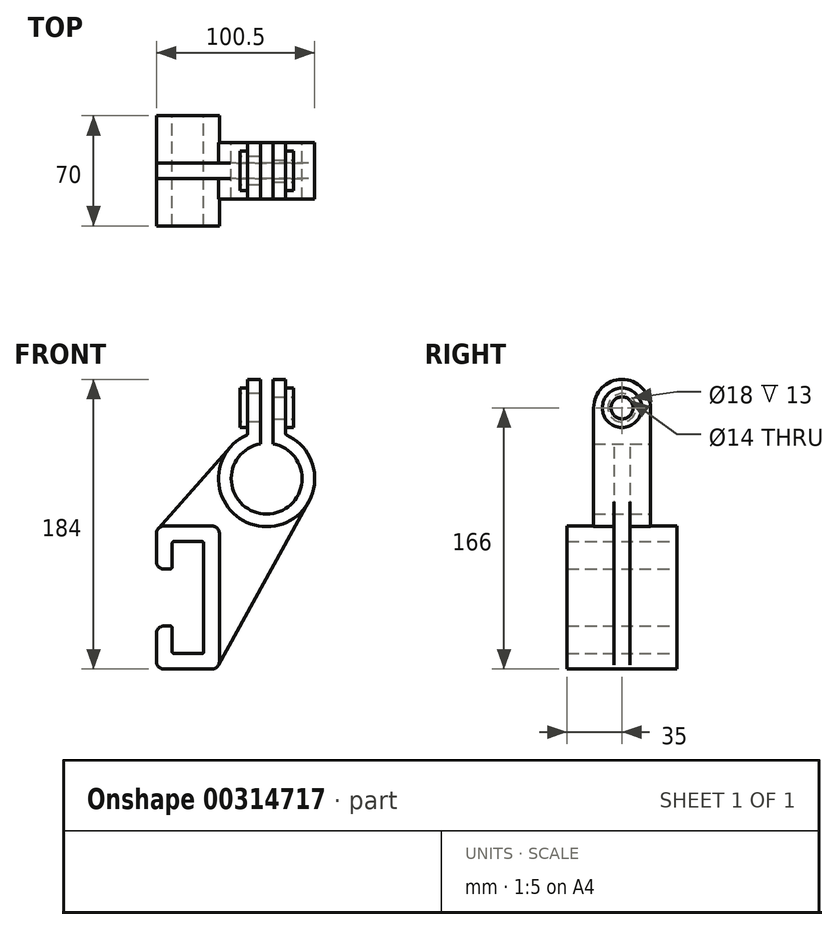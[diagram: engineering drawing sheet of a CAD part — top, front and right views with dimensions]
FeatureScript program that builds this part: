
annotation { "Feature Type Name" : "Feature", "Feature Type Description" : "" }
export const myFeature = defineFeature(function(context is Context, id is Id, definition is map)
    precondition{}
    {
        {
            var Q0;
            Q0=qCreatedBy(makeId("Front.planeOp"),FACE);
            var sketch = newSketch(context, id + "F0", { "sketchPlane" : qUnion([Q0])});
            skArc(sketch, "E0", {"start": v(-4, 22.14) * mm, "mid": v(0, -22.5) * mm, "end": v(4, 22.14) * mm});
            skLineSegment(sketch, "E1", {"start": v(0, 0) * mm, "end": v(0, 45) * mm, "construction": true});
            skLineSegment(sketch, "E2.0", {"start": v(-4, 22.14) * mm, "end": v(-4, 45) * mm});
            skLineSegment(sketch, "E3.0", {"start": v(4, 22.14) * mm, "end": v(4, 45) * mm});
            skLineSegment(sketch, "E4.0", {"start": v(12, 28.04) * mm, "end": v(12, 45) * mm});
            skArc(sketch, "E4.1", {"start": v(-12, 28.04) * mm, "mid": v(0, -30.5) * mm, "end": v(12, 28.04) * mm});
            skLineSegment(sketch, "E4.2", {"start": v(-12, 28.04) * mm, "end": v(-12, 45) * mm});
            skLineSegment(sketch, "E5", {"start": v(-12, 45) * mm, "end": v(-4, 45) * mm});
            skLineSegment(sketch, "E6", {"start": v(4, 45) * mm, "end": v(12, 45) * mm});
            skLineSegment(sketch, "E7.bottom", {"start": v(-40, -40) * mm, "end": v(-60, -40) * mm});
            skLineSegment(sketch, "E7.top", {"start": v(-40, -111) * mm, "end": v(-60, -111) * mm});
            skLineSegment(sketch, "E7.left", {"start": v(-40, -40) * mm, "end": v(-40, -111) * mm});
            skLineSegment(sketch, "E7.right", {"start": v(-60, -40) * mm, "end": v(-60, -57.5) * mm});
            skLineSegment(sketch, "E8.0", {"start": v(-70, -35) * mm, "end": v(-70, -52.5) * mm});
            skLineSegment(sketch, "E8.1", {"start": v(-35, -30) * mm, "end": v(-65, -30) * mm});
            skLineSegment(sketch, "E8.2", {"start": v(-30, -35) * mm, "end": v(-30, -116) * mm});
            skLineSegment(sketch, "E8.3", {"start": v(-35, -121) * mm, "end": v(-65, -121) * mm});
            skLineSegment(sketch, "E9", {"start": v(-60, -40) * mm, "end": v(-40, -111) * mm, "construction": true});
            skLineSegment(sketch, "E10.left", {"start": v(-100, -57.5) * mm, "end": v(-100, -93.5) * mm, "construction": true});
            skLineSegment(sketch, "E10.right", {"start": v(0, -57.5) * mm, "end": v(0, -93.5) * mm, "construction": true});
            skPoint(sketch, "E10.middle", {"position": v(-50, -75.5) * mm});
            skLineSegment(sketch, "E11.trimOffspring", {"start": v(-70, -98.5) * mm, "end": v(-70, -116) * mm});
            skLineSegment(sketch, "E12.trimOffspring", {"start": v(-60, -93.5) * mm, "end": v(-60, -111) * mm});
            skLineSegment(sketch, "E13", {"start": v(-65, -57.5) * mm, "end": v(-60, -57.5) * mm});
            skLineSegment(sketch, "E14", {"start": v(-65, -93.5) * mm, "end": v(-60, -93.5) * mm});
            skPoint(sketch, "E15.visualSharp", {"position": v(-70, -30) * mm});
            skArc(sketch, "E15.filletArc", {"start": v(-65, -30) * mm, "mid": v(-68.54, -31.46) * mm, "end": v(-70, -35) * mm});
            skPoint(sketch, "E16.visualSharp", {"position": v(-30, -30) * mm});
            skArc(sketch, "E16.filletArc", {"start": v(-30, -35) * mm, "mid": v(-31.46, -31.46) * mm, "end": v(-35, -30) * mm});
            skPoint(sketch, "E17.visualSharp", {"position": v(-30, -121) * mm});
            skArc(sketch, "E17.filletArc", {"start": v(-35, -121) * mm, "mid": v(-31.46, -119.54) * mm, "end": v(-30, -116) * mm});
            skPoint(sketch, "E18.visualSharp", {"position": v(-70, -121) * mm});
            skArc(sketch, "E18.filletArc", {"start": v(-70, -116) * mm, "mid": v(-68.54, -119.54) * mm, "end": v(-65, -121) * mm});
            skPoint(sketch, "E19.newPointB", {"position": v(-100, -93.5) * mm});
            skArc(sketch, "E19.filletArc", {"start": v(-65, -93.5) * mm, "mid": v(-68.54, -94.96) * mm, "end": v(-70, -98.5) * mm});
            skPoint(sketch, "E20.newPointB", {"position": v(-100, -57.5) * mm});
            skArc(sketch, "E20.filletArc", {"start": v(-70, -52.5) * mm, "mid": v(-68.54, -56.04) * mm, "end": v(-65, -57.5) * mm});
            skLineSegment(sketch, "E21.trimOffspring", {"start": v(-100, -57.5) * mm, "end": v(0, -57.5) * mm, "construction": true});
            skLineSegment(sketch, "E22.trimOffspring", {"start": v(-100, -93.5) * mm, "end": v(0, -93.5) * mm, "construction": true});
            skLineSegment(sketch, "E23", {"start": v(-22.85, 20.2) * mm, "end": v(-68.75, -31.69) * mm});
            skLineSegment(sketch, "E24", {"start": v(26.7, -14.76) * mm, "end": v(-30.62, -118.42) * mm});
            skSolve(sketch);
        }
        {
            var Q0;
            Q0=makeQuery(id+"F0.imprint","IMPRINT",FACE,{"disambiguationData":[TD([[makeQuery(id+"F0.imprint","IMPRINT",EDGE,{"derivedFrom":sQuery(id+"F0.wireOp",EDGE,"E0")}),-1.0]])]});
            extrude(context, id + "F1", {"entities" : qUnion([Q0]), "endBound" : BoundingType.SYMMETRIC, "depth" : 36 * mm});
        }
        {
            var Q0;
            {var subQ1=sQuery(id+"F0.wireOp",EDGE,"E8.1");Q0=makeQuery(id+"F0.imprint","IMPRINT",FACE,{"disambiguationData":[TD([[makeQuery(id+"F0.imprint","IMPRINT",EDGE,{"derivedFrom":subQ1}),-1.0]])]});}
            extrude(context, id + "F2", {"entities" : qUnion([Q0]), "operationType" : NewBodyOperationType.ADD, "endBound" : BoundingType.SYMMETRIC, "depth" : 10 * mm});
        }
        {
            var Q0;
            Q0=makeQuery(id+"F0.imprint","IMPRINT",FACE,{"disambiguationData":[TD([[makeQuery(id+"F0.imprint","IMPRINT",EDGE,{"derivedFrom":sQuery(id+"F0.wireOp",EDGE,"E7.bottom")}),-1.0]])]});
            extrude(context, id + "F3", {"entities" : qUnion([Q0]), "operationType" : NewBodyOperationType.ADD, "endBound" : BoundingType.SYMMETRIC, "depth" : 70 * mm});
        }
        {
            var Q0;
            Q0=qCreatedBy(makeId("Right.planeOp"),FACE);
            var sketch = newSketch(context, id + "F4", { "sketchPlane" : qUnion([Q0])});
            skLineSegment(sketch, "E25.0", {"start": v(-18, 45) * mm, "end": v(18, 45) * mm});
            skArc(sketch, "E26", {"start": v(18, 45) * mm, "mid": v(0, 63) * mm, "end": v(-18, 45) * mm});
            skSolve(sketch);
        }
        {
            var Q0;
            Q0=makeQuery(id+"F1.opExtrude","SWEPT_FACE",FACE,{"disambiguationData":[OSD([sQuery(id+"F0.wireOp",EDGE,"E4.0")])]});
            var sketch = newSketch(context, id + "F5", { "sketchPlane" : qUnion([Q0])});
            skArc(sketch, "E27.0", {"start": v(18, 45) * mm, "mid": v(0, 63) * mm, "end": v(-18, 45) * mm});
            skLineSegment(sketch, "E28.0", {"start": v(-18, 45) * mm, "end": v(18, 45) * mm});
            skSolve(sketch);
        }
        {
            var Q0;
            Q0 = qSketchRegion(id + "F5", true);
            var Q1;
            Q1=makeQuery(id+"F1.opExtrude","SWEPT_FACE",FACE,{"disambiguationData":[OSD([sQuery(id+"F0.wireOp",EDGE,"E3.0")])]});
            extrude(context, id + "F6", {"entities" : qUnion([Q0]), "operationType" : NewBodyOperationType.ADD, "endBound" : BoundingType.UP_TO_SURFACE, "oppositeDirection" : true, "endBoundEntityFace" : qUnion([Q1]), "depth" : 25 * mm});
        }
        {
            var Q0;
            Q0=makeQuery(id+"F1.opExtrude","SWEPT_FACE",FACE,{"disambiguationData":[OSD([sQuery(id+"F0.wireOp",EDGE,"E4.2")])]});
            var sketch = newSketch(context, id + "F7", { "sketchPlane" : qUnion([Q0])});
            skLineSegment(sketch, "E29.0.0", {"start": v(18, 45) * mm, "end": v(-18, 45) * mm});
            skArc(sketch, "E29.0.1", {"start": v(-18, 45) * mm, "mid": v(0, 63) * mm, "end": v(18, 45) * mm});
            skSolve(sketch);
        }
        {
            var Q0;
            Q0=makeQuery(id+"F7.imprint","IMPRINT",FACE,{"disambiguationData":[TD([[makeQuery(id+"F7.imprint","IMPRINT",EDGE,{"derivedFrom":sQuery(id+"F7.wireOp",EDGE,"E29.0.0")}),-1.0]])]});
            var Q1;
            Q1=makeQuery(id+"F1.opExtrude","SWEPT_FACE",FACE,{"disambiguationData":[OSD([sQuery(id+"F0.wireOp",EDGE,"E2.0")])]});
            extrude(context, id + "F8", {"entities" : qUnion([Q0]), "operationType" : NewBodyOperationType.ADD, "endBound" : BoundingType.UP_TO_SURFACE, "oppositeDirection" : true, "endBoundEntityFace" : qUnion([Q1]), "depth" : 25 * mm});
        }
        {
            var Q0;
            Q0=makeQuery(id+"F8.boolean.opBoolean","MERGE",FACE,{"derivedFrom":[makeQuery(id+"F1.opExtrude","SWEPT_FACE",FACE,{"disambiguationData":[OSD([sQuery(id+"F0.wireOp",EDGE,"E4.2")])]}),makeQuery(id+"F8.opExtrude","CAP_FACE",FACE,{"disambiguationData":[OSD([sQuery(id+"F7.wireOp",EDGE,"E29.0.0"),sQuery(id+"F7.wireOp",EDGE,"E29.0.1")])],"isStart":true})]});
            var sketch = newSketch(context, id + "F9", { "sketchPlane" : qUnion([Q0])});
            skPoint(sketch, "E30", {"position": v(0, 45) * mm});
            skCircle(sketch, "E31", {"center": v(0, 45) * mm, "radius": 12.5 * mm});
            skSolve(sketch);
        }
        {
            var Q0;
            Q0=makeQuery(id+"F9.imprint","IMPRINT",FACE,{"disambiguationData":[TD([[makeQuery(id+"F9.imprint","IMPRINT",EDGE,{"derivedFrom":sQuery(id+"F9.wireOp",EDGE,"E31")}),1.0]])]});
            extrude(context, id + "F10", {"entities" : qUnion([Q0]), "operationType" : NewBodyOperationType.ADD, "depth" : 5 * mm});
        }
        {
            var Q0;
            Q0=makeQuery(id+"F6.boolean.opBoolean","MERGE",FACE,{"derivedFrom":[makeQuery(id+"F1.opExtrude","SWEPT_FACE",FACE,{"disambiguationData":[OSD([sQuery(id+"F0.wireOp",EDGE,"E4.0")])]}),makeQuery(id+"F6.opExtrude","CAP_FACE",FACE,{"disambiguationData":[OSD([sQuery(id+"F5.wireOp",EDGE,"E27.0"),sQuery(id+"F5.wireOp",EDGE,"E28.0")])],"isStart":true})]});
            var sketch = newSketch(context, id + "F11", { "sketchPlane" : qUnion([Q0])});
            skCircle(sketch, "E32.0", {"center": v(0, 45) * mm, "radius": 12.5 * mm});
            skSolve(sketch);
        }
        {
            var Q0;
            Q0=makeQuery(id+"F11.imprint","IMPRINT",FACE,{"disambiguationData":[TD([[makeQuery(id+"F11.imprint","IMPRINT",EDGE,{"derivedFrom":sQuery(id+"F11.wireOp",EDGE,"E32.0")}),1.0]])]});
            extrude(context, id + "F12", {"entities" : qUnion([Q0]), "operationType" : NewBodyOperationType.ADD, "depth" : 5 * mm});
        }
        {
            var Q0;
            Q0=makeQuery(id+"F10.opExtrude","CAP_FACE",FACE,{"disambiguationData":[OSD([sQuery(id+"F9.wireOp",EDGE,"E31")])],"isStart":false});
            var sketch = newSketch(context, id + "F13", { "sketchPlane" : qUnion([Q0])});
            skPoint(sketch, "E33", {"position": v(0, 45) * mm});
            skSolve(sketch);
        }
        {
            var Q0;
            Q0=sQuery(id+"F13.wireOp",VERTEX,"E33");
            var Q1;
            Q1=makeQuery(id+"F1.opExtrude","SWEPT_BODY",BODY,{"disambiguationData":[OSD([sQuery(id+"F0.wireOp",EDGE,"E0"),sQuery(id+"F0.wireOp",EDGE,"E2.0"),sQuery(id+"F0.wireOp",EDGE,"E3.0"),sQuery(id+"F0.wireOp",EDGE,"E4.0"),sQuery(id+"F0.wireOp",EDGE,"E4.1"),sQuery(id+"F0.wireOp",EDGE,"E4.2"),sQuery(id+"F0.wireOp",EDGE,"E5"),sQuery(id+"F0.wireOp",EDGE,"E6")])]});
            hole(context, id + "F14", {"style" : HoleStyle.SIMPLE, "endStyle" : HoleEndStyle.BLIND, "holeDiameter" : 18 * mm, "holeDepth" : 18 * mm, "tappedDepth" : 12 * mm, "tapClearance" : 3, "locations" : qUnion([Q0]), "scope" : qUnion([Q1])});
        }
        {
            var Q0;
            Q0=makeQuery(id+"F12.opExtrude","CAP_FACE",FACE,{"disambiguationData":[OSD([sQuery(id+"F11.wireOp",EDGE,"E32.0")])],"isStart":false});
            var sketch = newSketch(context, id + "F15", { "sketchPlane" : qUnion([Q0])});
            skPoint(sketch, "E34", {"position": v(0, 45) * mm});
            skSolve(sketch);
        }
        {
            var Q0;
            Q0=sQuery(id+"F15.wireOp",VERTEX,"E34");
            var Q1;
            Q1=makeQuery(id+"F1.opExtrude","SWEPT_BODY",BODY,{"disambiguationData":[OSD([sQuery(id+"F0.wireOp",EDGE,"E0"),sQuery(id+"F0.wireOp",EDGE,"E2.0"),sQuery(id+"F0.wireOp",EDGE,"E3.0"),sQuery(id+"F0.wireOp",EDGE,"E4.0"),sQuery(id+"F0.wireOp",EDGE,"E4.1"),sQuery(id+"F0.wireOp",EDGE,"E4.2"),sQuery(id+"F0.wireOp",EDGE,"E5"),sQuery(id+"F0.wireOp",EDGE,"E6")])]});
            hole(context, id + "F16", {"style" : HoleStyle.SIMPLE, "endStyle" : HoleEndStyle.BLIND, "standardTappedOrClearance" : lookupTablePath({ "standard" : "ISO", "engagement" : "75%", "pitch" : "2 mm", "size" : "M16", "type" : "Tapped" }), "standardBlindInLast" : lookupTablePath({ "standard" : "ISO", "engagement" : "75%", "pitch" : "2 mm", "size" : "M16", "type" : "Tapped" }), "holeDiameter" : 14 * mm, "showTappedDepth" : true, "holeDepth" : 18 * mm, "tappedDepth" : 12 * mm, "tapClearance" : 3, "locations" : qUnion([Q0]), "scope" : qUnion([Q1]), "majorDiameter" : 16 * mm});
        }
        {
            var Q0;
            Q0=makeQuery(id+"F3.opExtrude","SWEPT_EDGE",EDGE,{"disambiguationData":[OSD([sQuery(id+"F0.wireOp",EDGE,"E7.bottom"),sQuery(id+"F0.wireOp",EDGE,"E7.right")])]});
            var Q1;
            Q1=makeQuery(id+"F3.opExtrude","SWEPT_EDGE",EDGE,{"disambiguationData":[OSD([sQuery(id+"F0.wireOp",EDGE,"E7.bottom"),sQuery(id+"F0.wireOp",EDGE,"E7.left")])]});
            var Q2;
            Q2=makeQuery(id+"F3.opExtrude","SWEPT_EDGE",EDGE,{"disambiguationData":[OSD([sQuery(id+"F0.wireOp",EDGE,"E7.top"),sQuery(id+"F0.wireOp",EDGE,"E7.left")])]});
            var Q3;
            Q3=makeQuery(id+"F3.opExtrude","SWEPT_EDGE",EDGE,{"disambiguationData":[OSD([sQuery(id+"F0.wireOp",EDGE,"E7.top"),sQuery(id+"F0.wireOp",EDGE,"E12.trimOffspring")])]});
            fillet(context, id + "F17", {"entities" : qUnion([Q0, Q1, Q2, Q3]), "radius" : 1 * mm, "tangentPropagation" : true, "allowEdgeOverflow" : false});
        }
        {
            var Q0;
            Q0=makeQuery(id+"F3.opExtrude","SWEPT_EDGE",EDGE,{"disambiguationData":[OSD([sQuery(id+"F0.wireOp",EDGE,"E7.right"),sQuery(id+"F0.wireOp",EDGE,"E13")])]});
            var Q1;
            Q1=makeQuery(id+"F3.opExtrude","SWEPT_EDGE",EDGE,{"disambiguationData":[OSD([sQuery(id+"F0.wireOp",EDGE,"E12.trimOffspring"),sQuery(id+"F0.wireOp",EDGE,"E14")])]});
            fillet(context, id + "F18", {"entities" : qUnion([Q0, Q1]), "radius" : 1.6 * mm, "tangentPropagation" : true, "allowEdgeOverflow" : false});
        }
        {
            var Q0;
            Q0=makeQuery(id+"F1.opExtrude","SWEPT_EDGE",EDGE,{"disambiguationData":[OSD([sQuery(id+"F0.wireOp",EDGE,"E4.0"),sQuery(id+"F0.wireOp",EDGE,"E4.1")])]});
            var Q1;
            Q1=makeQuery(id+"F1.opExtrude","SWEPT_EDGE",EDGE,{"disambiguationData":[OSD([sQuery(id+"F0.wireOp",EDGE,"E4.1"),sQuery(id+"F0.wireOp",EDGE,"E4.2")])]});
            fillet(context, id + "F19", {"entities" : qUnion([Q0, Q1]), "radius" : 1 * mm, "tangentPropagation" : true, "allowEdgeOverflow" : false});
        }
    });
